FCSTD DOCUMENT  (FreeCAD 0.14R3703 (Git))
Label: 7x5 pirate
License: CC-BY 3.0
LicenseURL: http://creativecommons.org/licenses/by/3.0/
objects: Sketcher::SketchObject×9
note: 9 computed .brp shape members not serialized (recipe doc carries the construction recipe); baked Part::Feature solids carry a one-line shape summary decoded from their .brp

FEATURE [Sketcher::SketchObject] Sketch  label="stemline"
  Placement = pos=(0,0,0) rot=(0.57735,0.57735,0.57735;2.0944rad)
  sketch-geometry (5):
    g0: LineSegment StartX=7.4597 StartY=9.43685 StartZ=0 EndX=14.127 EndY=19.4377 EndZ=0
    g1: LineSegment StartX=14.127 StartY=19.4377 StartZ=0 EndX=20.318 EndY=29.6767 EndZ=0
    g2: LineSegment StartX=20.318 StartY=29.6767 StartZ=0 EndX=25.0803 EndY=39.4395 EndZ=0
    g3: LineSegment StartX=25.0803 StartY=39.4395 StartZ=0 EndX=30.3189 EndY=50.1548 EndZ=0
    g4: LineSegment StartX=-0.049999 StartY=2.54488 StartZ=0 EndX=7.4597 EndY=9.43685 EndZ=0
  constraints (4):
    c: Coincident(g0,g1)
    c: Coincident(g1,g2)
    c: Coincident(g2,g3)
    c: Coincident(g0,g4)
FEATURE [Sketcher::SketchObject] Sketch001  label="cs1"
  Placement = pos=(0,0,0) rot=(1,0,0;1.5708rad)
  sketch-geometry (5):
    g0: LineSegment StartX=4.13472 StartY=7.67662 StartZ=0 EndX=6.40244 EndY=15.9916 EndZ=0
    g1: LineSegment StartX=6.40244 StartY=15.9916 StartZ=0 EndX=8.21661 EndY=22.7948 EndZ=0
    g2: LineSegment StartX=8.21661 StartY=22.7948 StartZ=0 EndX=9.42606 EndY=31.2609 EndZ=0
    g3: LineSegment StartX=9.42606 StartY=31.2609 StartZ=0 EndX=10.182 EndY=39.8783 EndZ=0
    g4: LineSegment StartX=-0.00751 StartY=2.64467 StartZ=0 EndX=4.13472 EndY=7.67662 EndZ=0
  constraints (4):
    c: Coincident(g0,g1)
    c: Coincident(g1,g2)
    c: Coincident(g2,g3)
    c: Coincident(g0,g4)
FEATURE [Sketcher::SketchObject] Sketch002  label="cs3"
  Placement = pos=(0,-20,-2) rot=(1,0,0;1.5708rad)
  sketch-geometry (5):
    g0: LineSegment StartX=0 StartY=0 StartZ=0 EndX=5.43729 EndY=6.96896 EndZ=0
    g1: LineSegment StartX=5.43729 StartY=6.96896 StartZ=0 EndX=9.08552 EndY=15.8869 EndZ=0
    g2: LineSegment StartX=9.08552 StartY=15.8869 StartZ=0 EndX=10.6502 EndY=22.1148 EndZ=0
    g3: LineSegment StartX=10.6502 StartY=22.1148 StartZ=0 EndX=11.9574 EndY=29.8925 EndZ=0
    g4: LineSegment StartX=11.9574 StartY=29.8925 StartZ=0 EndX=11.9882 EndY=29.9848 EndZ=0
  constraints (4):
    c: Coincident(g0,g1)
    c: Coincident(g1,g2)
    c: Coincident(g2,g3)
    c: Coincident(g3,g4)
FEATURE [Sketcher::SketchObject] Sketch003  label="transomXY"
  Placement = pos=(0,-65,0) rot=(0,0,1;0rad)
  sketch-geometry (5):
    g0: LineSegment StartX=-0.042821 StartY=-20.5374 StartZ=0 EndX=2.455 EndY=-20.5374 EndZ=0
    g1: LineSegment StartX=2.455 StartY=-20.5374 StartZ=0 EndX=5.43747 EndY=-20.4628 EndZ=0
    g2: LineSegment StartX=5.43747 StartY=-20.4628 StartZ=0 EndX=7.93528 EndY=-20.4255 EndZ=0
    g3: LineSegment StartX=7.93528 StartY=-20.4255 StartZ=0 EndX=10.5449 EndY=-20.3137 EndZ=0
    g4: LineSegment StartX=10.5449 StartY=-20.3137 StartZ=0 EndX=13.3037 EndY=-20.09 EndZ=0
  constraints (4):
    c: Coincident(g0,g1)
    c: Coincident(g1,g2)
    c: Coincident(g2,g3)
    c: Coincident(g3,g4)
FEATURE [Sketcher::SketchObject] Sketch008  label="cs7"
  Placement = pos=(0,-85,5) rot=(1,0,0;1.5708rad)
  sketch-geometry (5):
    g0: LineSegment StartX=7.80062 StartY=12.4181 StartZ=0 EndX=10.404 EndY=20.9938 EndZ=0
    g1: LineSegment StartX=10.404 StartY=20.9938 StartZ=0 EndX=11.8588 EndY=28.4975 EndZ=0
    g2: LineSegment StartX=11.8588 StartY=28.4975 StartZ=0 EndX=13.1604 EndY=36.1544 EndZ=0
    g3: LineSegment StartX=13.1604 StartY=36.1544 StartZ=0 EndX=14.2324 EndY=44.2706 EndZ=0
    g4: LineSegment StartX=0.143764 StartY=6.5989 StartZ=0 EndX=7.80062 EndY=12.4181 EndZ=0
  constraints (4):
    c: Coincident(g0,g1)
    c: Coincident(g1,g2)
    c: Coincident(g2,g3)
    c: Coincident(g0,g4)
FEATURE [Sketcher::SketchObject] Sketch009  label="cs2"
  Placement = pos=(0,-5,0) rot=(1,0,0;1.5708rad)
  sketch-geometry (5):
    g0: LineSegment StartX=0 StartY=0 StartZ=0 EndX=4.4325 EndY=6.75316 EndZ=0
    g1: LineSegment StartX=4.4325 StartY=6.75316 StartZ=0 EndX=7.93947 EndY=14.8594 EndZ=0
    g2: LineSegment StartX=7.93947 StartY=14.8594 StartZ=0 EndX=9.66421 EndY=21.5284 EndZ=0
    g3: LineSegment StartX=9.66421 StartY=21.5284 StartZ=0 EndX=11.1814 EndY=29.8536 EndZ=0
    g4: LineSegment StartX=11.1814 StartY=29.8536 StartZ=0 EndX=11.2021 EndY=29.9981 EndZ=0
  constraints (4):
    c: Coincident(g0,g1)
    c: Coincident(g1,g2)
    c: Coincident(g2,g3)
    c: Coincident(g3,g4)
FEATURE [Sketcher::SketchObject] Sketch010  label="cs4"
  Placement = pos=(0,-40,-2) rot=(1,0,0;1.5708rad)
  sketch-geometry (5):
    g0: LineSegment StartX=0 StartY=0 StartZ=0 EndX=5.43729 EndY=6.96896 EndZ=0
    g1: LineSegment StartX=5.43729 StartY=6.96896 StartZ=0 EndX=9.08552 EndY=15.8869 EndZ=0
    g2: LineSegment StartX=9.08552 StartY=15.8869 StartZ=0 EndX=10.6502 EndY=22.1148 EndZ=0
    g3: LineSegment StartX=10.6502 StartY=22.1148 StartZ=0 EndX=11.9882 EndY=29.8617 EndZ=0
    g4: LineSegment StartX=11.9882 StartY=29.8617 StartZ=0 EndX=11.9574 EndY=29.9848 EndZ=0
  constraints (4):
    c: Coincident(g0,g1)
    c: Coincident(g1,g2)
    c: Coincident(g2,g3)
    c: Coincident(g3,g4)
FEATURE [Sketcher::SketchObject] Sketch011  label="cs5"
  Placement = pos=(0,-60,0) rot=(1,0,0;1.5708rad)
  sketch-geometry (5):
    g0: LineSegment StartX=0 StartY=0 StartZ=0 EndX=5.0379 EndY=6.0726 EndZ=0
    g1: LineSegment StartX=5.0379 StartY=6.0726 StartZ=0 EndX=8.79381 EndY=14.8614 EndZ=0
    g2: LineSegment StartX=8.79381 StartY=14.8614 StartZ=0 EndX=10.5966 EndY=21.3216 EndZ=0
    g3: LineSegment StartX=10.5966 StartY=21.3216 StartZ=0 EndX=12.1741 EndY=29.9602 EndZ=0
    g4: LineSegment StartX=12.1741 StartY=29.9602 StartZ=0 EndX=12.1868 EndY=30.0169 EndZ=0
  constraints (4):
    c: Coincident(g0,g1)
    c: Coincident(g1,g2)
    c: Coincident(g2,g3)
    c: Coincident(g3,g4)
FEATURE [Sketcher::SketchObject] Sketch012  label="cs6"
  Placement = pos=(0,-65,0) rot=(1,0,0;1.5708rad)
  sketch-geometry (5):
    g0: LineSegment StartX=5.43729 StartY=6.96896 StartZ=0 EndX=9.08552 EndY=15.8869 EndZ=0
    g1: LineSegment StartX=9.08552 StartY=15.8869 StartZ=0 EndX=10.6502 EndY=22.1148 EndZ=0
    g2: LineSegment StartX=10.6502 StartY=22.1148 StartZ=0 EndX=12.1403 EndY=31.016 EndZ=0
    g3: LineSegment StartX=12.1403 StartY=31.016 StartZ=0 EndX=12.4507 EndY=40.8583 EndZ=0
    g4: LineSegment StartX=-0.027457 StartY=1.58212 StartZ=0 EndX=5.43729 EndY=6.96896 EndZ=0
  constraints (4):
    c: Coincident(g0,g1)
    c: Coincident(g1,g2)
    c: Coincident(g2,g3)
    c: Coincident(g0,g4)
